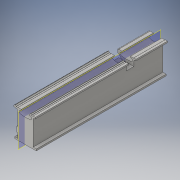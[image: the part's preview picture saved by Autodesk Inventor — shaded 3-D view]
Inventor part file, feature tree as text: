
AUTODESK INVENTOR PART (.ipt)
format: ipt  version: 2016 (Build 200138000, 138)  size: 347,136 bytes
history: native  units: in
note: dims shown in document units (in); Inventor stores cm internally (conversion verified against a paired STEP export)
features: extrude x8, sketch x8, chamfer x1, plane x1
ambient origin geometry x8: Origin, YZ Plane, XZ Plane, XY Plane, X Axis, Y Axis, Z Axis, Center Point
bodies: Solid1 (feature_tree)
feature tree (18):
  extrude  "Extrusion1"  TaperAngle=150.0deg  [1 undecoded]
  chamfer  "Chamfer1"  Distance=0.126in
  plane  "Work Plane3"
  extrude  "Extrusion2"  Depth=0.7874in
  extrude  "Extrusion3"  Depth=0.7874in
  extrude  "Extrusion4"  Depth=0.7874in
  extrude  "Extrusion5"  Depth=0.7874in
  extrude  "Extrusion6"  Depth=0.7874in
  extrude  "Extrusion7"  Depth=0.7874in
  extrude  "Extrusion8"  TaperAngle=120.0deg  [1 undecoded]
  sketch  "Sketch1"  dims[d0=0.4331in d1=150.0deg]
  sketch  "Sketch2"  dims[d2=0.3937in]
  sketch  "Sketch3"  dims[d3=0.4606in]
  sketch  "Sketch4"  dims[d4=0.4961in]
  sketch  "Sketch5"  dims[d5=0.962in]
  sketch  "Sketch6"  dims[d6=0.1496in]
  sketch  "Sketch7"  dims[d7=0.4016in]
  sketch  "Sketch8"  dims[d8=0.962in d9=0.126in d10=0.6339in d11=0.0787in d12=0.9921in d13=0.6181in d14=0.5787in d15=0.315in d16=120.0deg d17=0.1575in d18=2.4409in d19=8.0315in d22=3.6299in d24=0.5in d25=1.4252in d26=180.0deg d27=0.0787in d28=0.748in d29=0.0787in d30=0.5197in d31=0.962in d32=0.1811in d33=0.6299in d34=0.962in d35=0.5512in d36=0.5512in d37=90.0deg d38=0.1181in d39=60.0deg d40=0.7244in d41=0.8858in d42=0.374in d43=5.3543in d44=90.0deg d45=0.5118in d46=2.185in d47=90.0deg d50=90.0deg d51=1.378in d52=180.0deg d53=0.7087in d54=90.0deg d55=1.378in d57=0.7087in d58=0.4173in d59=180.0deg d60=0.315in d61=120.0deg d62=2.4409in d63=55.9055in d64=0.0in d65=0.3543in d66=0.0787in d67=45.0deg d68=40.1575in d69=3.2283in d70=3.4528in d71=55.9055in d72=0.0in d73=55.9055in d74=0.0in d75=55.9055in d76=0.0in d77=2.7953in d78=1.2205in d79=1.7323in d80=55.9055in d81=0.0in d82=1.0236in d83=0.0in d85=0.5118in d86=0.7283in d87=0.5512in d88=0.315in d89=0.315in d90=0.7874in d91=0.0in d92=0.8858in d93=0.5906in d94=0.315in d95=0.315in d96=6.7717in d97=0.7874in d98=0.0in]
note: 2 required parameter values undecoded (feature->parameter linkage not recoverable at this tier; creation-order binding heuristic only, values carry confidence <= 0.55)
